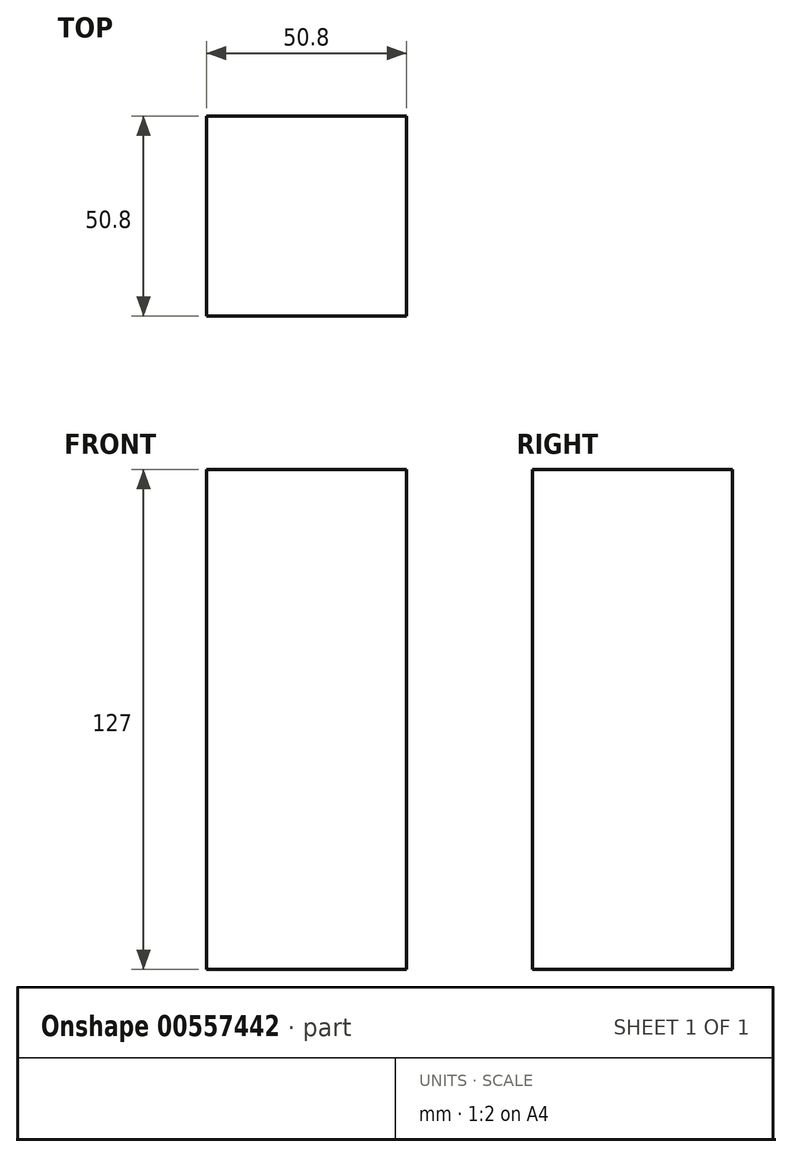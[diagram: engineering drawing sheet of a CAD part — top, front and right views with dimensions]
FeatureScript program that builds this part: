
annotation { "Feature Type Name" : "Feature", "Feature Type Description" : "" }
export const myFeature = defineFeature(function(context is Context, id is Id, definition is map)
    precondition{}
    {
        {
            var Q0;
            Q0=qCreatedBy(makeId("Front.planeOp"),FACE);
            var sketch = newSketch(context, id + "F0", { "sketchPlane" : qUnion([Q0])});
            skLineSegment(sketch, "E0.bottom", {"start": v(0, 127) * mm, "end": v(50.8, 127) * mm});
            skLineSegment(sketch, "E0.top", {"start": v(0, 0) * mm, "end": v(50.8, 0) * mm});
            skLineSegment(sketch, "E0.left", {"start": v(0, 127) * mm, "end": v(0, 0) * mm});
            skLineSegment(sketch, "E0.right", {"start": v(50.8, 127) * mm, "end": v(50.8, 0) * mm});
            skSolve(sketch);
        }
        {
            var Q0;
            Q0=makeQuery(id+"F0.imprint","IMPRINT",FACE,{"disambiguationData":[TD([[makeQuery(id+"F0.imprint","IMPRINT",EDGE,{"derivedFrom":sQuery(id+"F0.wireOp",EDGE,"E0.bottom")}),-1.0]])]});
            extrude(context, id + "F1", {"entities" : qUnion([Q0]), "depth" : 50.8 * mm, "offsetDistance" : 25.4 * mm});
        }
    });
